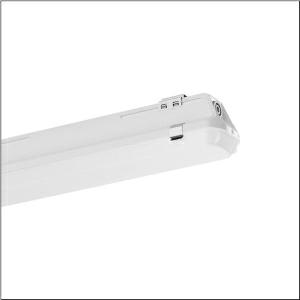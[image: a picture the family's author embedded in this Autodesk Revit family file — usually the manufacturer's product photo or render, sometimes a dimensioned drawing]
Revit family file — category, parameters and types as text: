
# Revit family: monsun_r__11_51fp10mp680h_8d08
name_source: partatom
category: Lighting Fixtures
units: mm (PartAtom-declared; Revit-internal decimal feet)

## family parameters
Cut with Voids When Loaded = No
Host = Face
Light Source = No
Part Type = Normal
Room Calculation Point = No
Round Connector Dimension = Use Diameter
Shared = No

## types (1)
- --- (1 x LED, 7970 lm, 45.4 W, 6500K)
    Apparent Load = 45 VA
    CIE Flux Codes = 47 77 93 94 100
    Color Rendering = 80
    Color Temperature = 6500K
    Default Elevation = 1800 mm
    Description = Monsun® 11, damp-proof luminaire, chain hanger, primary optical cover: enclosure, of PMMA, light emission: direct distribution, primary light characteristic: symmetric, installation type: suspended mounting, surface-mounted, horizontal mounting, vertical mounting, LED, rated luminous flux: 7.970lm, luminous efficacy: 176lm/W, light colour: 865, colour temperature: 6500K, control gear: ECG, with terminal, 3-pole, max. 2.5mm², mains connection: 220..240V, AC, 50/60Hz, rated input power: 45W, luminaire housing, of glass-fibre reinforced polyester, uncoated, bright grey, incl. chain hanger, length: 1.590mm, width: 90mm, height: 88mm, clip for enclosure, of stainless steel (V2A), ceiling mounting element, of stainless steel (V2A), chain hanger, of stainless steel (V2A), protection rating (complete): IP66, insulation class (complete): insulation class I (protective earthing), certification: CE, ENEC, VDE, UKCA, protection symbol: D, impact resistance: IK04, permissible operating ambient temperature: -35..+40°C, standard: EN 50419, EN 60598-2-1, no direct snow, no direct sun, no direct rain, for indoor or canopied outdoor use, corresponds to IFS (International Featured Standards) requirements for safety and quality in the food industry, contact your sales advisor before using the luminaires in applications with unclear chemical exposure, large temperature fluctuations or condensation-forming humidity, LABS conformity tested according to VDMA 24364:2018-05, packaging unit: 1 piece
    Height = 89 mm
    Lamp = 1 x LED
    Lamp Light Flux = 7970 lm
    Lamp Power = 45.4 W
    Lamp count = 1
    Length = 1590 mm
    Luminous efficacy = 176 lm/W
    Manufacturer = Siteco
    ModVariant = No
    Model = 51FP10MP680H
    Mounting Place = Ceiling
    Mounting Type = Surface mounted
    Number of Poles = 1
    OnlyDefault = Yes
    Power Factor = 1
    Product Name = Monsun® 11
    Product group = damp-proof luminaire
    ProductGroupID = 300
    Protection Class = Protection class I
    Protection Degree = IP 66
    RLX_Detail_Level = 1
    RLX_Emergency_Light_Flux = 0 lm
    RLX_Emergency_Type = 0
    RLX_Emergency_Type_DB = No
    RlxData = <blob elided: 89601 chars, md5=42b98e2b>
    Socket = socket
    Standby Power = 0 W
    System Light Flux = 7970 lm
    System Power = 45 W
    Type Comments = factory setting: luminous flux: 100 % | (A | C | E) | 105 mA
    Type Image = l_1004748.jpg
    URL = http://relux.com
    VarID = @adj_142477
    Voltage = 0 V
    Weight = 0.00 kg
    Width = 90 mm

## geometry (parser evidence)
native form markers: Blend x4, Sweep x13
no freeform markers — native parametric forms only
